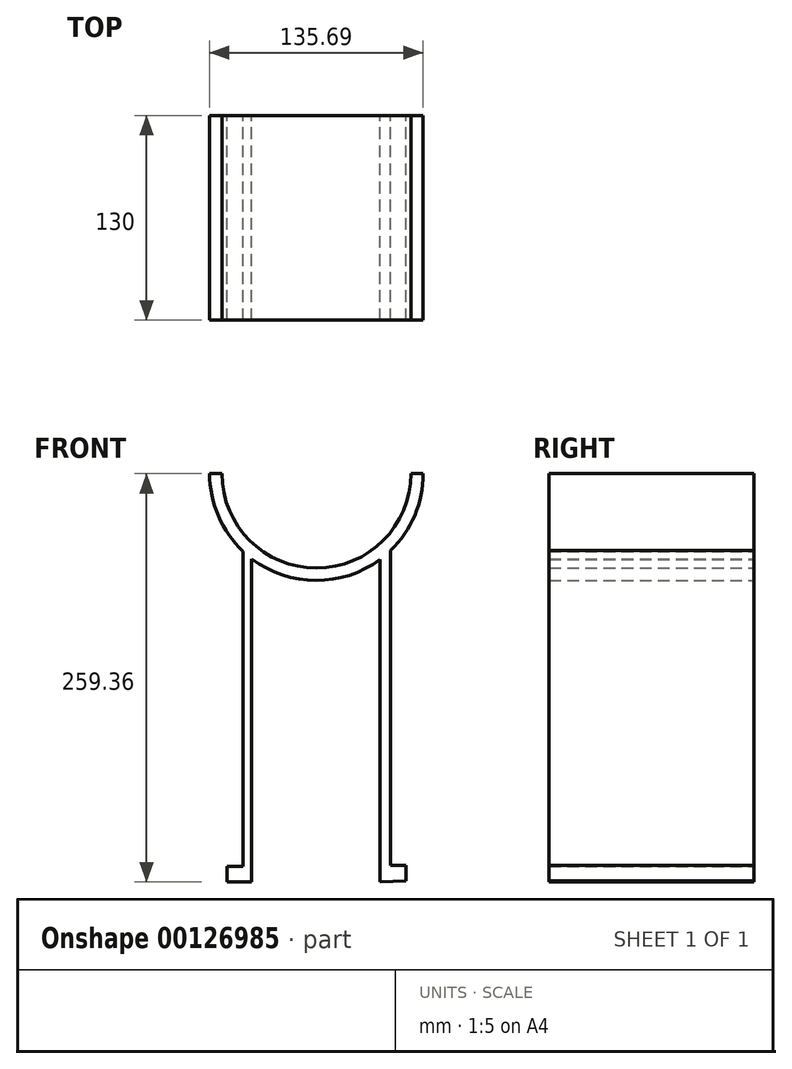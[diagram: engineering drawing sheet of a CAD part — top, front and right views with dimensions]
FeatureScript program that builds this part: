
annotation { "Feature Type Name" : "Feature", "Feature Type Description" : "" }
export const myFeature = defineFeature(function(context is Context, id is Id, definition is map)
    precondition{}
    {
        {
            var Q0;
            Q0=qCreatedBy(makeId("Front.planeOp"),FACE);
            var sketch = newSketch(context, id + "F0", { "sketchPlane" : qUnion([Q0])});
            skLineSegment(sketch, "E0", {"start": v(0, 0) * mm, "end": v(15.76, 0) * mm});
            skLineSegment(sketch, "E1", {"start": v(0, 0) * mm, "end": v(0, 10) * mm});
            skLineSegment(sketch, "E2.MirrorCS", {"start": v(113.57, 0.62) * mm, "end": v(113.57, 10.62) * mm});
            skArc(sketch, "E3", {"start": v(9.22, 222.8) * mm, "mid": v(56.78, 199.36) * mm, "end": v(104.35, 222.8) * mm});
            skPoint(sketch, "E4.orphan", {"position": v(15.76, 113.09) * mm});
            skPoint(sketch, "E5.orphan", {"position": v(97.81, 113.09) * mm});
            skArc(sketch, "E6", {"start": v(9.22, 222.8) * mm, "mid": v(-0.02, 240.05) * mm, "end": v(-3.22, 259.36) * mm});
            skArc(sketch, "E7", {"start": v(104.35, 222.8) * mm, "mid": v(113.6, 240.05) * mm, "end": v(116.78, 259.36) * mm});
            skArc(sketch, "E8", {"start": v(124.63, 259.36) * mm, "mid": v(56.78, 191.52) * mm, "end": v(-11.06, 259.36) * mm});
            skLineSegment(sketch, "E9", {"start": v(-11.06, 259.36) * mm, "end": v(-3.22, 259.36) * mm});
            skLineSegment(sketch, "E10", {"start": v(116.78, 259.36) * mm, "end": v(124.63, 259.36) * mm});
            skPoint(sketch, "E11.orphan", {"position": v(56.78, 0) * mm});
            skLineSegment(sketch, "E12", {"start": v(0, 10) * mm, "end": v(10.24, 10) * mm});
            skLineSegment(sketch, "E13", {"start": v(10.24, 10) * mm, "end": v(10.24, 210) * mm});
            skLineSegment(sketch, "E14", {"start": v(113.57, 10.62) * mm, "end": v(103.97, 10.62) * mm});
            skLineSegment(sketch, "E15", {"start": v(15.76, 0) * mm, "end": v(15.76, 205.33) * mm});
            skLineSegment(sketch, "E16", {"start": v(103.97, 10.62) * mm, "end": v(103.97, 210.62) * mm});
            skLineSegment(sketch, "E17", {"start": v(113.57, 0.62) * mm, "end": v(97.3, 0) * mm});
            skLineSegment(sketch, "E18", {"start": v(97.3, 0) * mm, "end": v(97.3, 204.95) * mm});
            skSolve(sketch);
        }
        {
            var Q0;
            Q0 = qSketchRegion(id + "F0", true);
            extrude(context, id + "F1", {"entities" : qUnion([Q0]), "depth" : 130 * mm});
        }
    });
